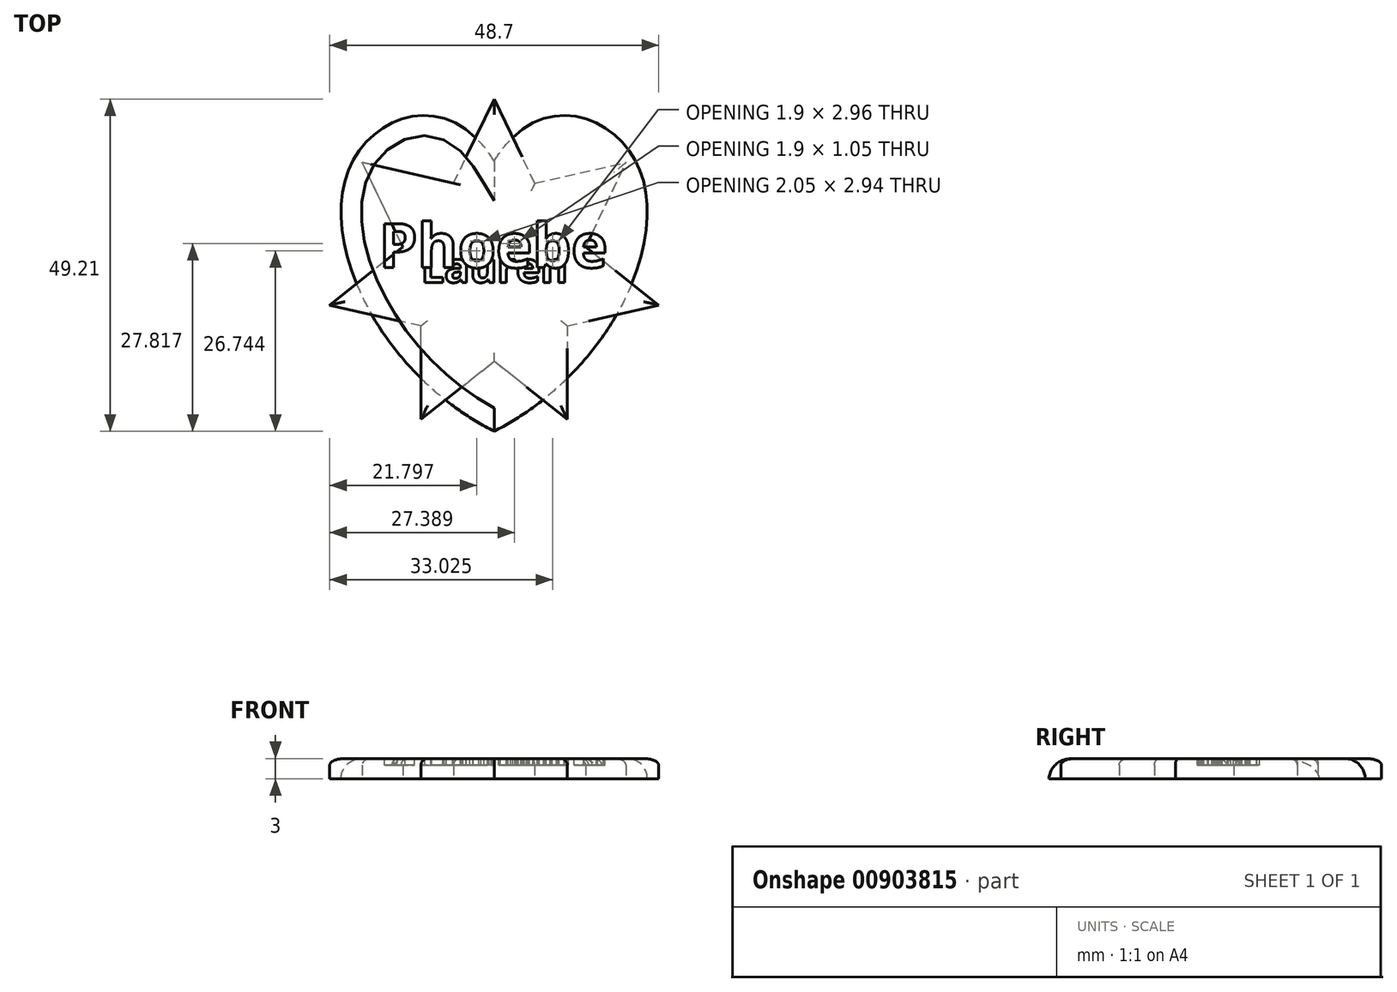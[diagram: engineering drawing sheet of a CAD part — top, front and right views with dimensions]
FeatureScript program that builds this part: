
annotation { "Feature Type Name" : "Feature", "Feature Type Description" : "" }
export const myFeature = defineFeature(function(context is Context, id is Id, definition is map)
    precondition{}
    {
        {
            var Q0;
            Q0=qCreatedBy(makeId("Top.planeOp"),FACE);
            var sketch = newSketch(context, id + "F0", { "sketchPlane" : qUnion([Q0])});
            skCircle(sketch, "E0.cCircle", {"center": v(0, 0) * mm, "radius": 22.5 * mm, "construction": true});
            skLineSegment(sketch, "E0.0", {"start": v(10.84, -22.5) * mm, "end": v(-10.84, -22.5) * mm, "construction": true});
            skLineSegment(sketch, "E0.1", {"start": v(-10.84, -22.5) * mm, "end": v(-24.35, -5.56) * mm, "construction": true});
            skLineSegment(sketch, "E0.2", {"start": v(-24.35, -5.56) * mm, "end": v(-19.52, 15.57) * mm, "construction": true});
            skLineSegment(sketch, "E0.3", {"start": v(-19.52, 15.57) * mm, "end": v(0, 24.97) * mm, "construction": true});
            skLineSegment(sketch, "E0.4", {"start": v(0, 24.97) * mm, "end": v(19.52, 15.57) * mm, "construction": true});
            skLineSegment(sketch, "E0.5", {"start": v(19.52, 15.57) * mm, "end": v(24.35, -5.56) * mm, "construction": true});
            skLineSegment(sketch, "E0.6", {"start": v(24.35, -5.56) * mm, "end": v(10.84, -22.5) * mm, "construction": true});
            skPoint(sketch, "E0.0.midPoint", {"position": v(0, -22.5) * mm});
            skCircle(sketch, "E1.cCircle", {"center": v(0, 0) * mm, "radius": 12.5 * mm, "construction": true});
            skLineSegment(sketch, "E1.0", {"start": v(-6.02, 12.5) * mm, "end": v(6.02, 12.5) * mm, "construction": true});
            skLineSegment(sketch, "E1.1", {"start": v(6.02, 12.5) * mm, "end": v(13.53, 3.09) * mm, "construction": true});
            skLineSegment(sketch, "E1.2", {"start": v(13.53, 3.09) * mm, "end": v(10.85, -8.65) * mm, "construction": true});
            skLineSegment(sketch, "E1.3", {"start": v(10.85, -8.65) * mm, "end": v(0, -13.87) * mm, "construction": true});
            skLineSegment(sketch, "E1.4", {"start": v(0, -13.87) * mm, "end": v(-10.85, -8.65) * mm, "construction": true});
            skLineSegment(sketch, "E1.5", {"start": v(-10.85, -8.65) * mm, "end": v(-13.53, 3.09) * mm, "construction": true});
            skLineSegment(sketch, "E1.6", {"start": v(-13.53, 3.09) * mm, "end": v(-6.02, 12.5) * mm, "construction": true});
            skPoint(sketch, "E1.0.midPoint", {"position": v(0, 12.5) * mm});
            skLineSegment(sketch, "E2", {"start": v(10.85, -8.65) * mm, "end": v(10.84, -22.5) * mm});
            skLineSegment(sketch, "E3", {"start": v(10.84, -22.5) * mm, "end": v(0, -13.87) * mm});
            skLineSegment(sketch, "E4", {"start": v(-10.84, -22.5) * mm, "end": v(0, -13.87) * mm});
            skLineSegment(sketch, "E5", {"start": v(-10.84, -22.5) * mm, "end": v(-10.85, -8.65) * mm});
            skLineSegment(sketch, "E6", {"start": v(-10.85, -8.65) * mm, "end": v(-24.35, -5.56) * mm});
            skLineSegment(sketch, "E7", {"start": v(-13.53, 3.09) * mm, "end": v(-24.35, -5.56) * mm});
            skLineSegment(sketch, "E8", {"start": v(-13.53, 3.09) * mm, "end": v(-19.52, 15.57) * mm});
            skLineSegment(sketch, "E9", {"start": v(-6.02, 12.5) * mm, "end": v(-19.52, 15.57) * mm});
            skLineSegment(sketch, "E10", {"start": v(-6.02, 12.5) * mm, "end": v(0, 24.97) * mm});
            skLineSegment(sketch, "E11", {"start": v(6.02, 12.5) * mm, "end": v(0, 24.97) * mm});
            skLineSegment(sketch, "E12", {"start": v(13.53, 3.09) * mm, "end": v(19.52, 15.57) * mm});
            skLineSegment(sketch, "E13", {"start": v(6.02, 12.5) * mm, "end": v(19.52, 15.57) * mm});
            skLineSegment(sketch, "E14", {"start": v(13.53, 3.09) * mm, "end": v(24.35, -5.56) * mm});
            skLineSegment(sketch, "E15", {"start": v(10.85, -8.65) * mm, "end": v(24.35, -5.56) * mm});
            skSolve(sketch);
        }
        {
            var Q0;
            Q0 = qSketchRegion(id + "F0", true);
            extrude(context, id + "F1", {"entities" : qUnion([Q0]), "depth" : 3 * mm, "offsetDistance" : 25 * mm});
        }
        {
            var Q0;
            Q0=makeQuery(id+"F1.opExtrude","CAP_FACE",FACE,{"disambiguationData":[OSD([sQuery(id+"F0.wireOp",EDGE,"E2"),sQuery(id+"F0.wireOp",EDGE,"E3"),sQuery(id+"F0.wireOp",EDGE,"E4"),sQuery(id+"F0.wireOp",EDGE,"E5"),sQuery(id+"F0.wireOp",EDGE,"E6"),sQuery(id+"F0.wireOp",EDGE,"E7"),sQuery(id+"F0.wireOp",EDGE,"E8"),sQuery(id+"F0.wireOp",EDGE,"E9"),sQuery(id+"F0.wireOp",EDGE,"E10"),sQuery(id+"F0.wireOp",EDGE,"E11"),sQuery(id+"F0.wireOp",EDGE,"E12"),sQuery(id+"F0.wireOp",EDGE,"E13"),sQuery(id+"F0.wireOp",EDGE,"E14"),sQuery(id+"F0.wireOp",EDGE,"E15")])],"isStart":false});
            var sketch = newSketch(context, id + "F2", { "sketchPlane" : qUnion([Q0])});
            skText(sketch, "E16", { "text": "Lauren", "fontName": "OpenSans-Bold.ttf"});
            skPoint(sketch, "E16.firstSnap0", {"position": v(10.84, -15.58) * mm});
            const initialGuessF2  = {"E16": [-0.01084, -0.0022, 1, 0, 0.00444]};
            skSetInitialGuess(sketch, initialGuessF2);
            skSolve(sketch);
        }
        {
            var Q0;
            Q0 = qSketchRegion(id + "F2", true);
            extrude(context, id + "F3", {"entities" : qUnion([Q0]), "operationType" : NewBodyOperationType.REMOVE, "oppositeDirection" : true, "depth" : 1 * mm, "offsetDistance" : 25 * mm});
        }
        {
            var Q0;
            Q0=makeQuery(id+"F1.opExtrude","CAP_EDGE",EDGE,{"disambiguationData":[OSD([sQuery(id+"F0.wireOp",EDGE,"E15")])],"isStart":false});
            var Q1;
            Q1=makeQuery(id+"F1.opExtrude","CAP_EDGE",EDGE,{"disambiguationData":[OSD([sQuery(id+"F0.wireOp",EDGE,"E2")])],"isStart":false});
            var Q2;
            Q2=makeQuery(id+"F1.opExtrude","CAP_EDGE",EDGE,{"disambiguationData":[OSD([sQuery(id+"F0.wireOp",EDGE,"E3")])],"isStart":false});
            var Q3;
            Q3=makeQuery(id+"F1.opExtrude","CAP_EDGE",EDGE,{"disambiguationData":[OSD([sQuery(id+"F0.wireOp",EDGE,"E4")])],"isStart":false});
            var Q4;
            Q4=makeQuery(id+"F1.opExtrude","CAP_EDGE",EDGE,{"disambiguationData":[OSD([sQuery(id+"F0.wireOp",EDGE,"E5")])],"isStart":false});
            var Q5;
            Q5=makeQuery(id+"F1.opExtrude","CAP_EDGE",EDGE,{"disambiguationData":[OSD([sQuery(id+"F0.wireOp",EDGE,"E6")])],"isStart":false});
            var Q6;
            Q6=makeQuery(id+"F1.opExtrude","CAP_EDGE",EDGE,{"disambiguationData":[OSD([sQuery(id+"F0.wireOp",EDGE,"E7")])],"isStart":false});
            var Q7;
            Q7=makeQuery(id+"F1.opExtrude","CAP_EDGE",EDGE,{"disambiguationData":[OSD([sQuery(id+"F0.wireOp",EDGE,"E8")])],"isStart":false});
            var Q8;
            Q8=makeQuery(id+"F1.opExtrude","CAP_EDGE",EDGE,{"disambiguationData":[OSD([sQuery(id+"F0.wireOp",EDGE,"E10")])],"isStart":false});
            var Q9;
            Q9=makeQuery(id+"F1.opExtrude","CAP_EDGE",EDGE,{"disambiguationData":[OSD([sQuery(id+"F0.wireOp",EDGE,"E11")])],"isStart":false});
            var Q10;
            Q10=makeQuery(id+"F1.opExtrude","CAP_EDGE",EDGE,{"disambiguationData":[OSD([sQuery(id+"F0.wireOp",EDGE,"E13")])],"isStart":false});
            var Q11;
            Q11=makeQuery(id+"F1.opExtrude","CAP_EDGE",EDGE,{"disambiguationData":[OSD([sQuery(id+"F0.wireOp",EDGE,"E12")])],"isStart":false});
            var Q12;
            Q12=makeQuery(id+"F1.opExtrude","CAP_EDGE",EDGE,{"disambiguationData":[OSD([sQuery(id+"F0.wireOp",EDGE,"E14")])],"isStart":false});
            fillet(context, id + "F4", {"entities" : qUnion([Q0, Q1, Q2, Q3, Q4, Q5, Q6, Q7, Q8, Q9, Q10, Q11, Q12]), "radius" : 1 * mm, "tangentPropagation" : true, "allowEdgeOverflow" : false});
        }
        {
            var Q0;
            Q0=qCreatedBy(makeId("Top.planeOp"),FACE);
            var sketch = newSketch(context, id + "F5", { "sketchPlane" : qUnion([Q0])});
            skLineSegment(sketch, "E17", {"start": v(0, 15.76) * mm, "end": v(0, -24.24) * mm, "construction": true});
            skFitSpline(sketch, "E18", {"points": [v(0, 15.76) * mm, v(21, 15.68) * mm, v(0, -24.24) * mm], "startDerivative": vector(46.83, 78.27) * mm, "endDerivative": vector(-87.73, -44.52) * mm});
            skFitSpline(sketch, "E19.MirrorCS", {"points": [v(0, 15.76) * mm, v(-21, 15.68) * mm, v(0, -24.24) * mm], "startDerivative": vector(-46.83, 78.27) * mm, "endDerivative": vector(87.73, -44.52) * mm});
            skSolve(sketch);
        }
        {
            var Q0;
            Q0 = qSketchRegion(id + "F5", true);
            extrude(context, id + "F6", {"entities" : qUnion([Q0]), "depth" : 3 * mm, "offsetDistance" : 25 * mm});
        }
        {
            var Q0;
            Q0=makeQuery(id+"F6.opExtrude","CAP_EDGE",EDGE,{"disambiguationData":[OSD([sQuery(id+"F5.wireOp",EDGE,"E19.MirrorCS")])],"isStart":false});
            var Q1;
            Q1=makeQuery(id+"F6.opExtrude","CAP_EDGE",EDGE,{"disambiguationData":[OSD([sQuery(id+"F5.wireOp",EDGE,"E18")])],"isStart":false});
            fillet(context, id + "F7", {"entities" : qUnion([Q0, Q1]), "radius" : 3 * mm, "tangentPropagation" : true, "allowEdgeOverflow" : false});
        }
        {
            var Q0;
            Q0=makeQuery(id+"F6.opExtrude","CAP_FACE",FACE,{"disambiguationData":[OSD([sQuery(id+"F5.wireOp",EDGE,"E18"),sQuery(id+"F5.wireOp",EDGE,"E19.MirrorCS")])],"isStart":false});
            var sketch = newSketch(context, id + "F8", { "sketchPlane" : qUnion([Q0])});
            skText(sketch, "E20", { "text": "Phoebe", "fontName": "OpenSans-Bold.ttf"});
            const initialGuessF8  = {"E20": [-0.01708, 0, 1, 0, 0.00656]};
            skSetInitialGuess(sketch, initialGuessF8);
            skSolve(sketch);
        }
        {
            var Q0;
            Q0 = qSketchRegion(id + "F8", true);
            extrude(context, id + "F9", {"entities" : qUnion([Q0]), "operationType" : NewBodyOperationType.REMOVE, "oppositeDirection" : true, "depth" : 1 * mm, "offsetDistance" : 25 * mm});
        }
    });
